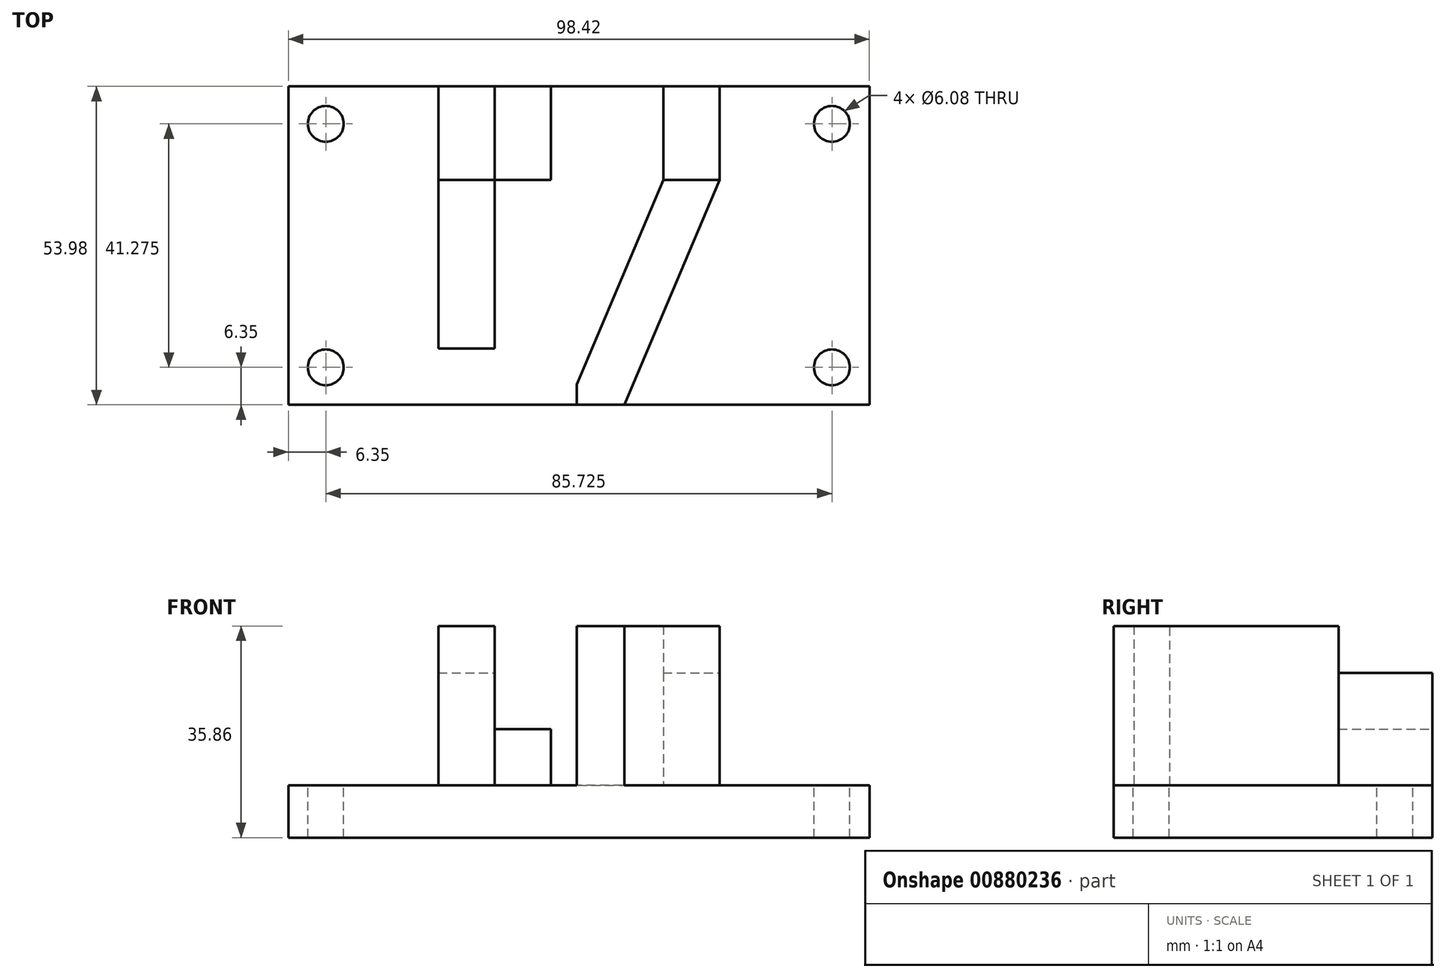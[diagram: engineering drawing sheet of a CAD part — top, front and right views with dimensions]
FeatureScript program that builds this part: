
annotation { "Feature Type Name" : "Feature", "Feature Type Description" : "" }
export const myFeature = defineFeature(function(context is Context, id is Id, definition is map)
    precondition{}
    {
        {
            var Q0;
            Q0=qCreatedBy(makeId("Top.planeOp"),FACE);
            var sketch = newSketch(context, id + "F0", { "sketchPlane" : qUnion([Q0])});
            skLineSegment(sketch, "E0.bottom", {"start": v(0, 0) * mm, "end": v(98.42, 0) * mm});
            skLineSegment(sketch, "E0.top", {"start": v(0, 53.97) * mm, "end": v(98.42, 53.97) * mm});
            skLineSegment(sketch, "E0.left", {"start": v(0, 0) * mm, "end": v(0, 53.97) * mm});
            skLineSegment(sketch, "E0.right", {"start": v(98.42, 0) * mm, "end": v(98.42, 53.97) * mm});
            skSolve(sketch);
        }
        {
            var Q0;
            Q0=qSketchRegion(id+"F0",true);
            extrude(context, id + "F1", {"entities" : qUnion([Q0]), "depth" : 8.9 * mm});
        }
        {
            var Q0;
            Q0=makeQuery(id+"F1.opExtrude","CAP_FACE",FACE,{"disambiguationData":[OSD([sQuery(id+"F0.wireOp",EDGE,"E0.bottom"),sQuery(id+"F0.wireOp",EDGE,"E0.top"),sQuery(id+"F0.wireOp",EDGE,"E0.left"),sQuery(id+"F0.wireOp",EDGE,"E0.right")])],"isStart":false});
            var sketch = newSketch(context, id + "F2", { "sketchPlane" : qUnion([Q0])});
            skLineSegment(sketch, "E1", {"start": v(34.93, 0) * mm, "end": v(34.92, 38.1) * mm});
            skLineSegment(sketch, "E2", {"start": v(34.92, 38.1) * mm, "end": v(44.45, 38.1) * mm});
            skLineSegment(sketch, "E3", {"start": v(44.45, 38.1) * mm, "end": v(44.45, 53.97) * mm});
            skLineSegment(sketch, "E4", {"start": v(25.4, 0) * mm, "end": v(25.4, 53.97) * mm});
            skLineSegment(sketch, "E5", {"start": v(25.4, 53.97) * mm, "end": v(44.45, 53.97) * mm});
            skLineSegment(sketch, "E6", {"start": v(25.4, 0) * mm, "end": v(34.93, 0) * mm});
            skSolve(sketch);
        }
        {
            var Q0;
            Q0=makeQuery(id+"F2.imprint","IMPRINT",FACE,{"disambiguationData":[TD([[makeQuery(id+"F2.imprint","IMPRINT",EDGE,{"derivedFrom":sQuery(id+"F2.wireOp",EDGE,"E1")}),1.0]])]});
            extrude(context, id + "F3", {"entities" : qUnion([Q0]), "operationType" : NewBodyOperationType.ADD, "depth" : 9.52 * mm});
        }
        {
            var Q0;
            {var subQ0=sQuery(id+"F0.wireOp",EDGE,"E0.top");var subQ1=sQuery(id+"F0.wireOp",EDGE,"E0.right");var subQ2=sQuery(id+"F0.wireOp",EDGE,"E0.bottom");Q0=makeQuery(id+"F3.boolean.opBoolean","SPLIT",FACE,{"disambiguationData":[TD([makeQuery(id+"F1.opExtrude","SWEPT_FACE",FACE,{"disambiguationData":[OSD([subQ1])]})])],"derivedFrom":makeQuery(id+"F1.opExtrude","CAP_FACE",FACE,{"disambiguationData":[OSD([subQ2,subQ0,sQuery(id+"F0.wireOp",EDGE,"E0.left"),subQ1])],"isStart":false})});}
            var sketch = newSketch(context, id + "F4", { "sketchPlane" : qUnion([Q0])});
            skLineSegment(sketch, "E7", {"start": v(63.5, 53.97) * mm, "end": v(63.5, 38.1) * mm});
            skLineSegment(sketch, "E8", {"start": v(73.03, 38.1) * mm, "end": v(73.03, 53.97) * mm});
            skLineSegment(sketch, "E9", {"start": v(73.03, 53.97) * mm, "end": v(63.5, 53.98) * mm});
            skLineSegment(sketch, "E10", {"start": v(63.5, 38.1) * mm, "end": v(48.87, 3.42) * mm});
            skLineSegment(sketch, "E11", {"start": v(48.87, 3.42) * mm, "end": v(48.87, 0) * mm});
            skLineSegment(sketch, "E12", {"start": v(48.87, 0) * mm, "end": v(56.95, 0) * mm});
            skLineSegment(sketch, "E13", {"start": v(56.95, 0) * mm, "end": v(73.03, 38.1) * mm});
            skSolve(sketch);
        }
        {
            var Q0;
            Q0=qSketchRegion(id+"F4",true);
            extrude(context, id + "F5", {"entities" : qUnion([Q0]), "operationType" : NewBodyOperationType.ADD, "depth" : 19.05 * mm});
        }
        {
            var Q0;
            Q0=makeQuery(id+"F5.opExtrude","CAP_FACE",FACE,{"disambiguationData":[OSD([sQuery(id+"F4.wireOp",EDGE,"E7"),sQuery(id+"F4.wireOp",EDGE,"E8"),sQuery(id+"F4.wireOp",EDGE,"E9"),sQuery(id+"F4.wireOp",EDGE,"E10"),sQuery(id+"F4.wireOp",EDGE,"E11"),sQuery(id+"F4.wireOp",EDGE,"E12"),sQuery(id+"F4.wireOp",EDGE,"E13")])],"isStart":false});
            var sketch = newSketch(context, id + "F6", { "sketchPlane" : qUnion([Q0])});
            skLineSegment(sketch, "E14.0", {"start": v(56.95, 0) * mm, "end": v(73.03, 38.1) * mm});
            skLineSegment(sketch, "E15.0", {"start": v(63.5, 38.1) * mm, "end": v(48.87, 3.42) * mm});
            skLineSegment(sketch, "E16", {"start": v(63.5, 38.1) * mm, "end": v(73.03, 38.1) * mm});
            skLineSegment(sketch, "E17.0", {"start": v(48.87, 0) * mm, "end": v(56.95, 0) * mm});
            skLineSegment(sketch, "E18.0", {"start": v(48.87, 3.42) * mm, "end": v(48.87, 0) * mm});
            skSolve(sketch);
        }
        {
            var Q0;
            Q0=qSketchRegion(id+"F6",true);
            extrude(context, id + "F7", {"entities" : qUnion([Q0]), "operationType" : NewBodyOperationType.ADD, "depth" : 7.92 * mm});
        }
        {
            var Q0;
            Q0=makeQuery(id+"F3.opExtrude","CAP_FACE",FACE,{"disambiguationData":[OSD([sQuery(id+"F2.wireOp",EDGE,"E1"),sQuery(id+"F2.wireOp",EDGE,"E2"),sQuery(id+"F2.wireOp",EDGE,"E3"),sQuery(id+"F2.wireOp",EDGE,"E4"),sQuery(id+"F2.wireOp",EDGE,"E5"),sQuery(id+"F2.wireOp",EDGE,"E6")])],"isStart":false});
            var sketch = newSketch(context, id + "F8", { "sketchPlane" : qUnion([Q0])});
            skLineSegment(sketch, "E19.bottom", {"start": v(34.93, 0) * mm, "end": v(25.4, 0) * mm});
            skLineSegment(sketch, "E19.top", {"start": v(34.92, 53.97) * mm, "end": v(25.4, 53.97) * mm});
            skLineSegment(sketch, "E19.left", {"start": v(34.93, 0) * mm, "end": v(34.92, 53.97) * mm});
            skLineSegment(sketch, "E19.right", {"start": v(25.4, 0) * mm, "end": v(25.4, 53.97) * mm});
            skSolve(sketch);
        }
        {
            var Q0;
            Q0=qSketchRegion(id+"F8",true);
            extrude(context, id + "F9", {"entities" : qUnion([Q0]), "operationType" : NewBodyOperationType.ADD, "depth" : 9.52 * mm});
        }
        {
            var Q0;
            Q0=makeQuery(id+"F9.opExtrude","CAP_FACE",FACE,{"disambiguationData":[OSD([sQuery(id+"F8.wireOp",EDGE,"E19.bottom"),sQuery(id+"F8.wireOp",EDGE,"E19.top"),sQuery(id+"F8.wireOp",EDGE,"E19.left"),sQuery(id+"F8.wireOp",EDGE,"E19.right")])],"isStart":false});
            var sketch = newSketch(context, id + "F10", { "sketchPlane" : qUnion([Q0])});
            skLineSegment(sketch, "E20.bottom", {"start": v(34.92, 0) * mm, "end": v(25.4, 0) * mm});
            skLineSegment(sketch, "E20.top", {"start": v(34.92, 38.1) * mm, "end": v(25.4, 38.1) * mm});
            skLineSegment(sketch, "E20.left", {"start": v(34.92, 0) * mm, "end": v(34.92, 38.1) * mm});
            skLineSegment(sketch, "E20.right", {"start": v(25.4, 0) * mm, "end": v(25.4, 38.1) * mm});
            skSolve(sketch);
        }
        {
            var Q0;
            Q0=qSketchRegion(id+"F10",true);
            extrude(context, id + "F11", {"entities" : qUnion([Q0]), "operationType" : NewBodyOperationType.ADD, "depth" : 7.92 * mm});
        }
        {
            var Q0;
            {var subQ0=sQuery(id+"F0.wireOp",EDGE,"E0.left");var subQ1=sQuery(id+"F0.wireOp",EDGE,"E0.top");var subQ2=sQuery(id+"F0.wireOp",EDGE,"E0.bottom");Q0=makeQuery(id+"F3.boolean.opBoolean","SPLIT",FACE,{"disambiguationData":[TD([makeQuery(id+"F1.opExtrude","SWEPT_FACE",FACE,{"disambiguationData":[OSD([subQ0])]})])],"derivedFrom":makeQuery(id+"F1.opExtrude","CAP_FACE",FACE,{"disambiguationData":[OSD([subQ2,subQ1,subQ0,sQuery(id+"F0.wireOp",EDGE,"E0.right")])],"isStart":false})});}
            var sketch = newSketch(context, id + "F12", { "sketchPlane" : qUnion([Q0])});
            skCircle(sketch, "E21", {"center": v(6.35, 47.62) * mm, "radius": 3.04 * mm});
            skCircle(sketch, "E22", {"center": v(6.35, 6.35) * mm, "radius": 3.04 * mm});
            skCircle(sketch, "E23", {"center": v(92.08, 6.35) * mm, "radius": 3.04 * mm});
            skCircle(sketch, "E24", {"center": v(92.08, 47.62) * mm, "radius": 3.04 * mm});
            skSolve(sketch);
        }
        {
            var Q0;
            Q0=qSketchRegion(id+"F12",true);
            extrude(context, id + "F13", {"entities" : qUnion([Q0]), "operationType" : NewBodyOperationType.REMOVE, "oppositeDirection" : true, "depth" : 25.4 * mm});
        }
        {
            var Q0;
            Q0=makeQuery(id+"F11.opExtrude","CAP_FACE",FACE,{"disambiguationData":[OSD([sQuery(id+"F10.wireOp",EDGE,"E20.bottom"),sQuery(id+"F10.wireOp",EDGE,"E20.top"),sQuery(id+"F10.wireOp",EDGE,"E20.left"),sQuery(id+"F10.wireOp",EDGE,"E20.right")])],"isStart":false});
            var sketch = newSketch(context, id + "F14", { "sketchPlane" : qUnion([Q0])});
            skLineSegment(sketch, "E25.bottom", {"start": v(25.4, 0) * mm, "end": v(34.93, 0) * mm});
            skLineSegment(sketch, "E25.top", {"start": v(25.4, 9.53) * mm, "end": v(34.93, 9.53) * mm});
            skLineSegment(sketch, "E25.left", {"start": v(25.4, 0) * mm, "end": v(25.4, 9.53) * mm});
            skLineSegment(sketch, "E25.right", {"start": v(34.93, 0) * mm, "end": v(34.93, 9.53) * mm});
            skSolve(sketch);
        }
        {
            var Q0;
            Q0=qSketchRegion(id+"F14",true);
            var Q1;
            {var subQ0=sQuery(id+"F0.wireOp",EDGE,"E0.left");var subQ1=sQuery(id+"F0.wireOp",EDGE,"E0.top");var subQ2=sQuery(id+"F0.wireOp",EDGE,"E0.bottom");Q1=makeQuery(id+"F3.boolean.opBoolean","SPLIT",FACE,{"disambiguationData":[TD([makeQuery(id+"F1.opExtrude","SWEPT_FACE",FACE,{"disambiguationData":[OSD([subQ0])]})])],"derivedFrom":makeQuery(id+"F1.opExtrude","CAP_FACE",FACE,{"disambiguationData":[OSD([subQ2,subQ1,subQ0,sQuery(id+"F0.wireOp",EDGE,"E0.right")])],"isStart":false})});}
            extrude(context, id + "F15", {"entities" : qUnion([Q0]), "operationType" : NewBodyOperationType.REMOVE, "endBound" : BoundingType.UP_TO_SURFACE, "oppositeDirection" : true, "endBoundEntityFace" : qUnion([Q1]), "depth" : 25.4 * mm});
        }
    });
